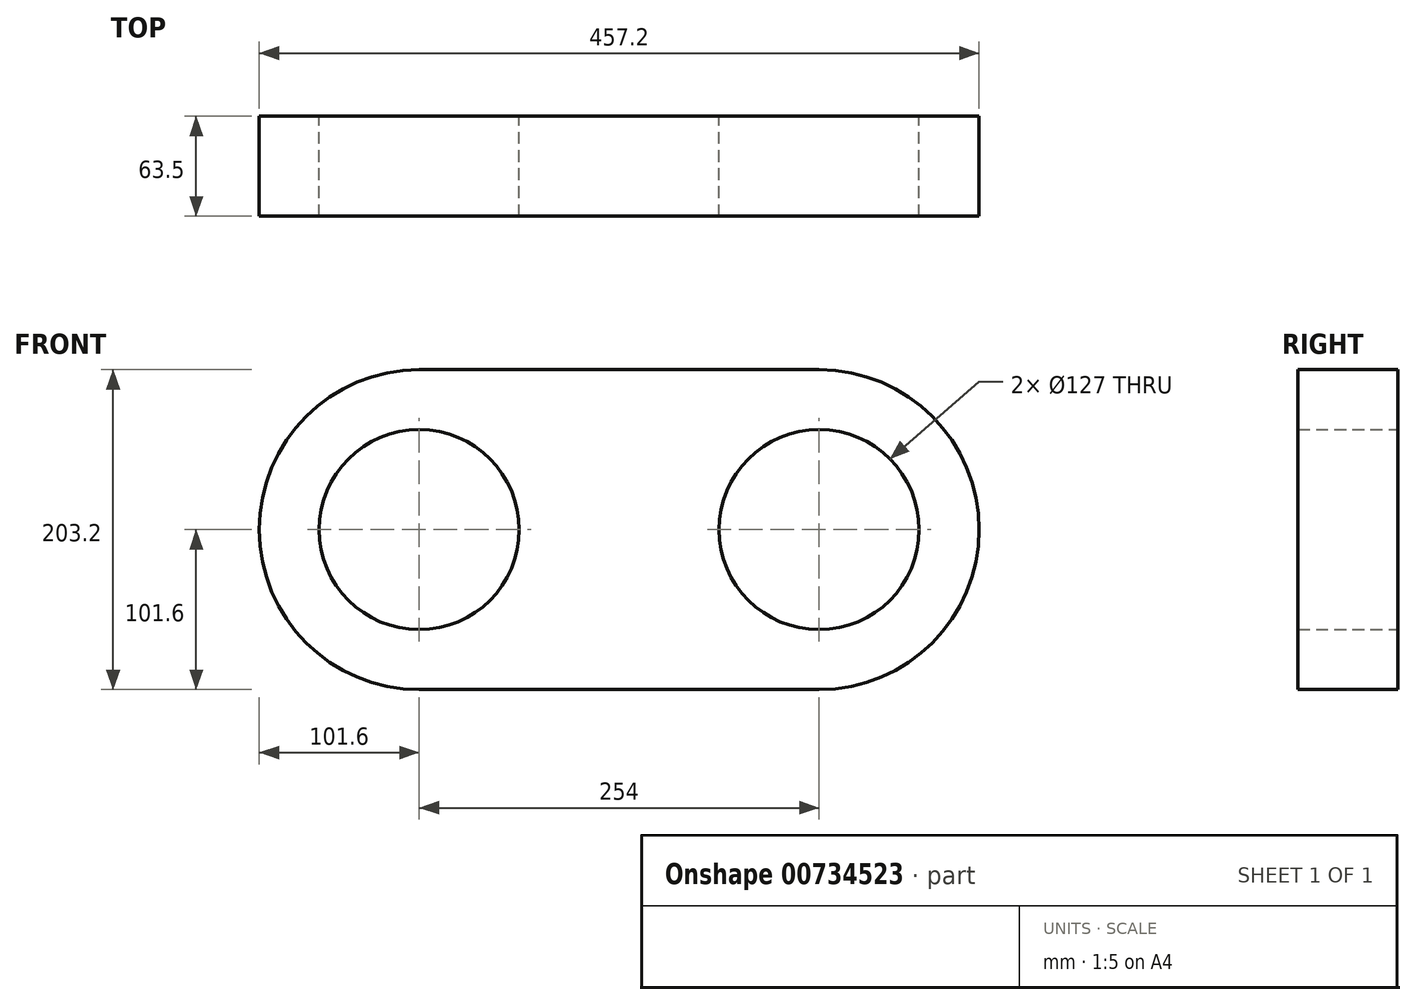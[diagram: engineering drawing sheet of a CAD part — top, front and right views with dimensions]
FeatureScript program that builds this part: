
annotation { "Feature Type Name" : "Feature", "Feature Type Description" : "" }
export const myFeature = defineFeature(function(context is Context, id is Id, definition is map)
    precondition{}
    {
        {
            var Q0;
            Q0=qCreatedBy(makeId("Front.planeOp"),FACE);
            var sketch = newSketch(context, id + "F0", { "sketchPlane" : qUnion([Q0])});
            skLineSegment(sketch, "E0", {"start": v(0, 0) * mm, "end": v(254, 0) * mm, "construction": true});
            skArc(sketch, "E1", {"start": v(0, 101.6) * mm, "mid": v(-101.6, 0) * mm, "end": v(0, -101.6) * mm});
            skArc(sketch, "E2", {"start": v(254, -101.6) * mm, "mid": v(355.6, 0) * mm, "end": v(254, 101.6) * mm});
            skLineSegment(sketch, "E3.0", {"start": v(0, -101.6) * mm, "end": v(254, -101.6) * mm});
            skLineSegment(sketch, "E4.0", {"start": v(0, 101.6) * mm, "end": v(254, 101.6) * mm});
            skCircle(sketch, "E5", {"center": v(0, 0) * mm, "radius": 63.5 * mm});
            skCircle(sketch, "E6", {"center": v(254, 0) * mm, "radius": 63.5 * mm});
            skSolve(sketch);
        }
        {
            var Q0;
            Q0 = qSketchRegion(id + "F0", true);
            extrude(context, id + "F1", {"entities" : qUnion([Q0]), "depth" : 63.5 * mm, "offsetDistance" : 25.4 * mm});
        }
    });
